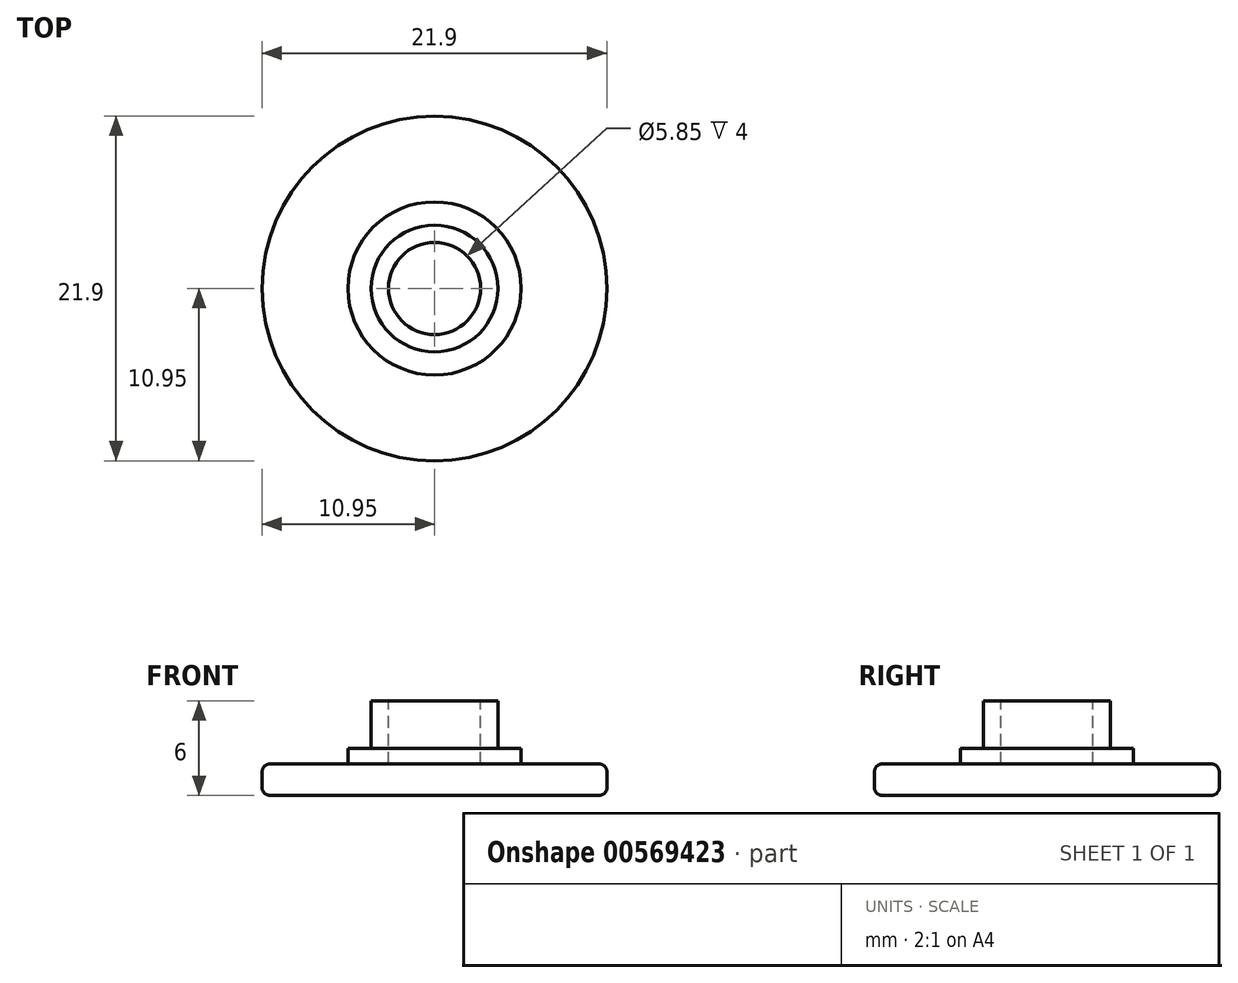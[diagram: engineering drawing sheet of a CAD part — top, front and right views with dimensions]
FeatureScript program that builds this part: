
annotation { "Feature Type Name" : "Feature", "Feature Type Description" : "" }
export const myFeature = defineFeature(function(context is Context, id is Id, definition is map)
    precondition{}
    {
        {
            var Q0;
            Q0=qCreatedBy(makeId("Top.planeOp"),FACE);
            var sketch = newSketch(context, id + "F0", { "sketchPlane" : qUnion([Q0])});
            skCircle(sketch, "E0", {"center": v(0, 0) * mm, "radius": 0.07 * mm});
            skCircle(sketch, "E1", {"center": v(0, 0) * mm, "radius": 10.95 * mm});
            skSolve(sketch);
        }
        {
            var Q0;
            Q0=qCreatedBy(makeId("Top.planeOp"),FACE);
            var sketch = newSketch(context, id + "F1", { "sketchPlane" : qUnion([Q0])});
            skCircle(sketch, "E2", {"center": v(0, 0) * mm, "radius": 5.5 * mm});
            skSolve(sketch);
        }
        {
            var Q0;
            Q0=qCreatedBy(makeId("Top.planeOp"),FACE);
            var sketch = newSketch(context, id + "F2", { "sketchPlane" : qUnion([Q0])});
            skCircle(sketch, "E3", {"center": v(0, 0) * mm, "radius": 4.03 * mm});
            skSolve(sketch);
        }
        {
            var Q0;
            Q0=qSketchRegion(id+"F0",true);
            extrude(context, id + "F3", {"entities" : qUnion([Q0]), "depth" : 2 * mm});
        }
        {
            var Q0;
            Q0=qSketchRegion(id+"F1",true);
            extrude(context, id + "F4", {"entities" : qUnion([Q0]), "operationType" : NewBodyOperationType.ADD, "depth" : 3 * mm});
        }
        {
            var Q0;
            Q0=qSketchRegion(id+"F2",true);
            extrude(context, id + "F5", {"entities" : qUnion([Q0]), "operationType" : NewBodyOperationType.ADD, "depth" : 6 * mm});
        }
        {
            var Q0;
            Q0=makeQuery(id+"F3.opExtrude","SWEPT_FACE",FACE,{"disambiguationData":[OSD([sQuery(id+"F0.wireOp",EDGE,"E1")])]});
            fillet(context, id + "F6", {"entities" : qUnion([Q0]), "radius" : .5 * mm, "tangentPropagation" : true, "allowEdgeOverflow" : false});
        }
        {
            var Q0;
            Q0=makeQuery(id+"F5.opExtrude","CAP_FACE",FACE,{"disambiguationData":[OSD([sQuery(id+"F2.wireOp",EDGE,"E3")])],"isStart":false});
            var sketch = newSketch(context, id + "F7", { "sketchPlane" : qUnion([Q0])});
            skCircle(sketch, "E4.0", {"center": v(0, 0) * mm, "radius": 2.92 * mm});
            skSolve(sketch);
        }
        {
            var Q0;
            Q0=qSketchRegion(id+"F7",true);
            extrude(context, id + "F8", {"entities" : qUnion([Q0]), "operationType" : NewBodyOperationType.REMOVE, "oppositeDirection" : true, "depth" : 4 * mm});
        }
    });
